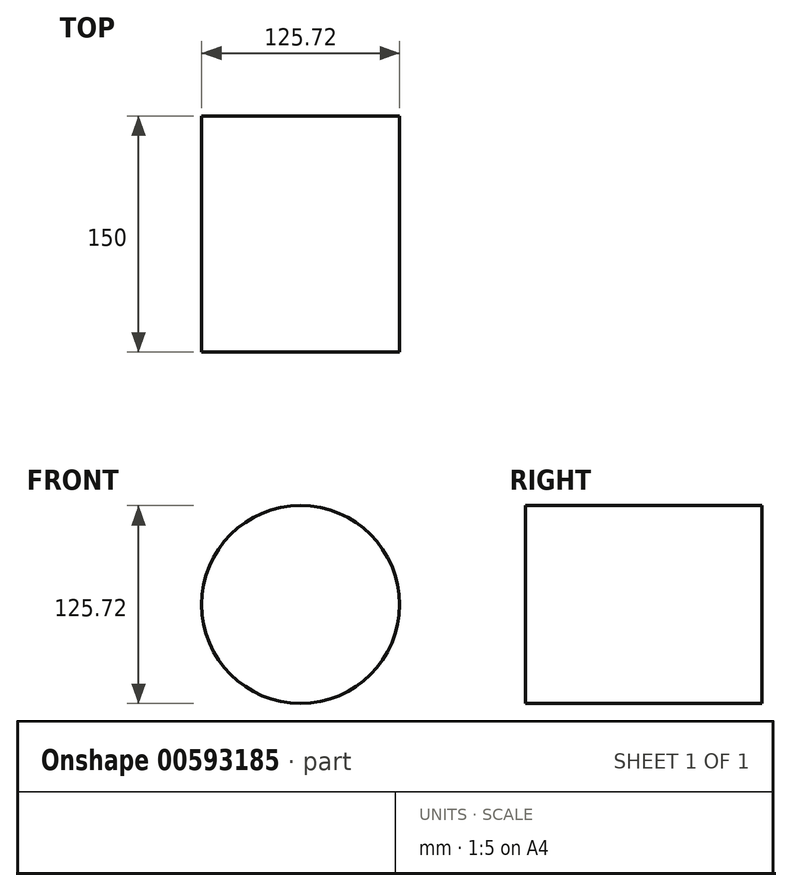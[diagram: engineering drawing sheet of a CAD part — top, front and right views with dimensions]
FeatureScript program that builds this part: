
annotation { "Feature Type Name" : "Feature", "Feature Type Description" : "" }
export const myFeature = defineFeature(function(context is Context, id is Id, definition is map)
    precondition{}
    {
        {
            var Q0;
            Q0=qCreatedBy(makeId("Front.planeOp"),FACE);
            var sketch = newSketch(context, id + "F0", { "sketchPlane" : qUnion([Q0])});
            skCircle(sketch, "E0", {"center": v(0, 0) * mm, "radius": 62.86 * mm});
            skSolve(sketch);
        }
        {
            var Q0;
            Q0=makeQuery(id+"F0.imprint","IMPRINT",FACE,{"disambiguationData":[TD([[makeQuery(id+"F0.imprint","IMPRINT",EDGE,{"derivedFrom":sQuery(id+"F0.wireOp",EDGE,"E0")}),1.0]])]});
            extrude(context, id + "F1", {"entities" : qUnion([Q0]), "depth" : 150 * mm, "offsetDistance" : 25 * mm});
        }
        {
            var Q0;
            Q0=makeQuery(id+"F1.opExtrude","CAP_FACE",FACE,{"disambiguationData":[OSD([sQuery(id+"F0.wireOp",EDGE,"E0")])],"isStart":false});
            var sketch = newSketch(context, id + "F2", { "sketchPlane" : qUnion([Q0])});
            skCircle(sketch, "E1", {"center": v(0, 0) * mm, "radius": 41.12 * mm});
            skSolve(sketch);
        }
        {
            var Q0;
            Q0=makeQuery(id+"F2.imprint","IMPRINT",FACE,{"disambiguationData":[TD([[makeQuery(id+"F2.imprint","IMPRINT",EDGE,{"derivedFrom":sQuery(id+"F2.wireOp",EDGE,"E1")}),1.0]])]});
            extrude(context, id + "F3", {"entities" : qUnion([Q0]), "operationType" : NewBodyOperationType.ADD, "oppositeDirection" : true, "depth" : 50 * mm, "offsetDistance" : 25 * mm});
        }
    });
